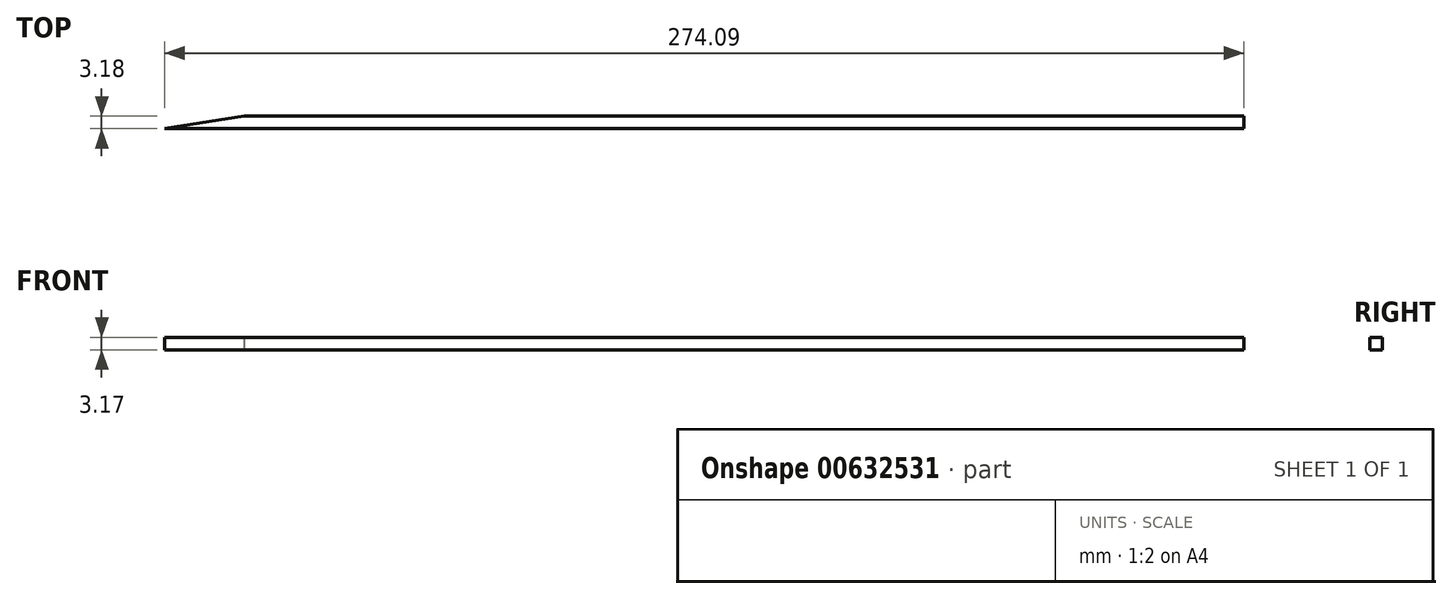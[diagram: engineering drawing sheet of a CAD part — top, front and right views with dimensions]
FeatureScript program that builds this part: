
annotation { "Feature Type Name" : "Feature", "Feature Type Description" : "" }
export const myFeature = defineFeature(function(context is Context, id is Id, definition is map)
    precondition{}
    {
        {
            var Q0;
            Q0=qCreatedBy(makeId("Top.planeOp"),FACE);
            var sketch = newSketch(context, id + "F0", { "sketchPlane" : qUnion([Q0])});
            skLineSegment(sketch, "E0", {"start": v(-2.79, 9.27) * mm, "end": v(251.21, 9.27) * mm});
            skLineSegment(sketch, "E1", {"start": v(251.21, 9.27) * mm, "end": v(251.21, 6.1) * mm});
            skLineSegment(sketch, "E2", {"start": v(251.21, 6.1) * mm, "end": v(-22.88, 6.1) * mm});
            skLineSegment(sketch, "E3", {"start": v(-22.88, 6.1) * mm, "end": v(-2.79, 9.27) * mm});
            skSolve(sketch);
        }
        {
            var Q0;
            Q0=makeQuery(id+"F0.imprint","IMPRINT",FACE,{"disambiguationData":[TD([[makeQuery(id+"F0.imprint","IMPRINT",EDGE,{"derivedFrom":sQuery(id+"F0.wireOp",EDGE,"E0")}),-1.0]])]});
            extrude(context, id + "F1", {"entities" : qUnion([Q0]), "depth" : 3.17 * mm, "offsetDistance" : 25.4 * mm});
        }
    });
